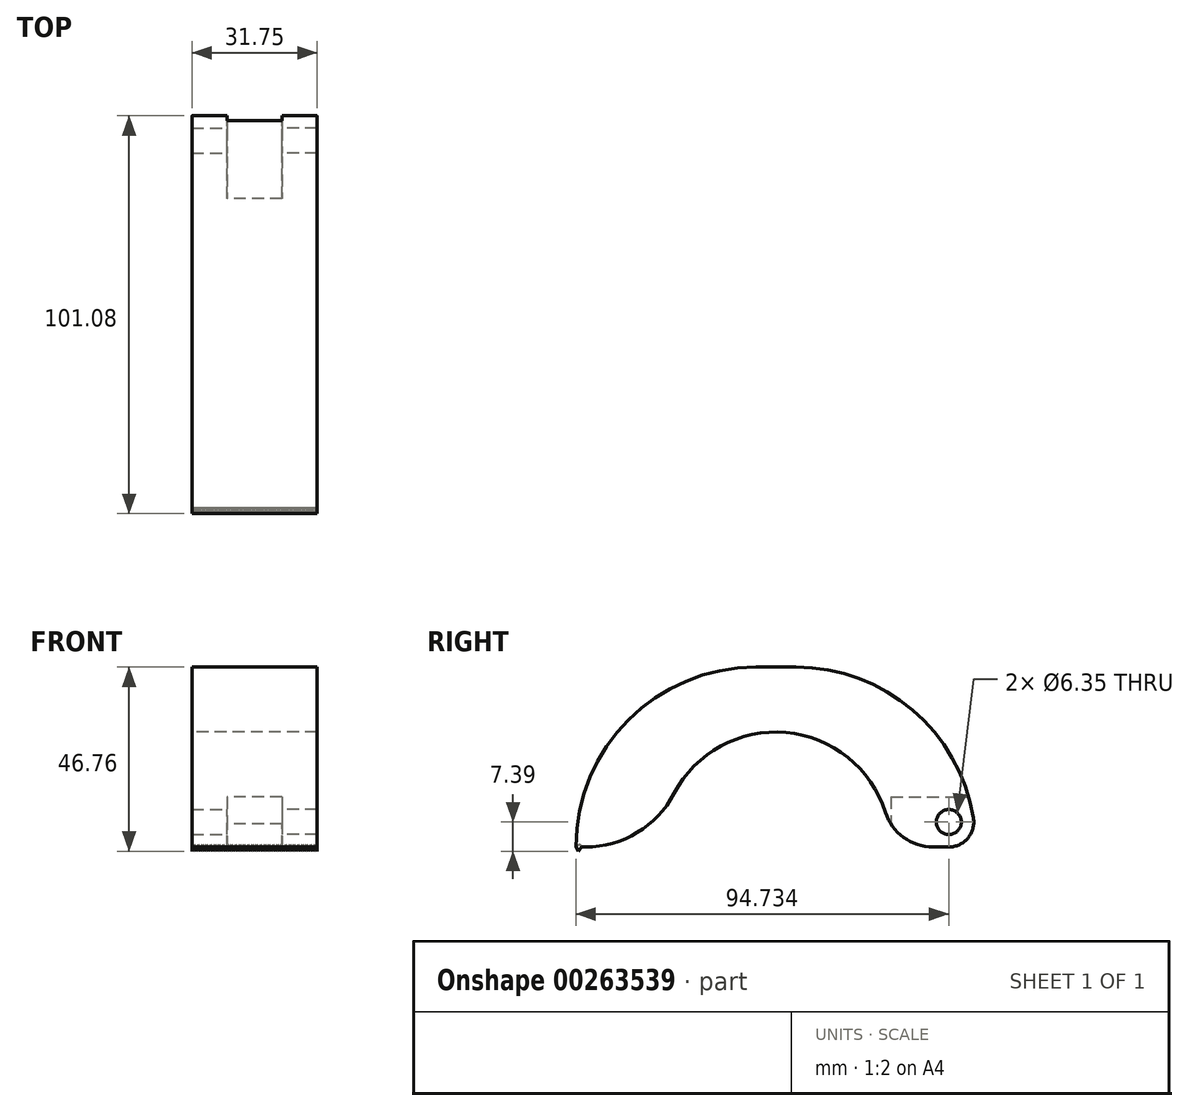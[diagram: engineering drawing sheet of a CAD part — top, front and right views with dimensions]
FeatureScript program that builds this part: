
annotation { "Feature Type Name" : "Feature", "Feature Type Description" : "" }
export const myFeature = defineFeature(function(context is Context, id is Id, definition is map)
    precondition{}
    {
        {
            var Q0;
            Q0=qCreatedBy(makeId("Right.planeOp"),FACE);
            var sketch = newSketch(context, id + "F0", { "sketchPlane" : qUnion([Q0])});
            skLineSegment(sketch, "E0.bottom", {"start": v(-5.08, 22.86) * mm, "end": v(5.08, 22.86) * mm});
            skLineSegment(sketch, "E0.top", {"start": v(-50.8, -22.86) * mm, "end": v(-48.34, -22.86) * mm});
            skLineSegment(sketch, "E0.left", {"start": v(-50.8, -22.86) * mm, "end": v(-50.8, -22.86) * mm});
            skLineSegment(sketch, "E0.right", {"start": v(50.8, -22.86) * mm, "end": v(50.8, -22.86) * mm});
            skPoint(sketch, "E0.middle", {"position": v(0, 0) * mm});
            skArc(sketch, "E1", {"start": v(27.84, -14) * mm, "mid": v(2.57, 6.24) * mm, "end": v(-25.86, -9.27) * mm});
            skLineSegment(sketch, "E2.trimOffspring", {"start": v(39.94, -22.86) * mm, "end": v(50.8, -22.86) * mm});
            skLineSegment(sketch, "E3", {"start": v(50.8, -22.86) * mm, "end": v(-50.8, -22.86) * mm, "construction": true});
            skPoint(sketch, "E4.visualSharp", {"position": v(50.8, 22.86) * mm});
            skArc(sketch, "E4.filletArc", {"start": v(50.8, -22.86) * mm, "mid": v(37.4, 9.47) * mm, "end": v(5.08, 22.86) * mm});
            skPoint(sketch, "E5.visualSharp", {"position": v(-50.8, 22.86) * mm});
            skArc(sketch, "E5.filletArc", {"start": v(-5.08, 22.86) * mm, "mid": v(-37.4, 9.47) * mm, "end": v(-50.8, -22.86) * mm});
            skPoint(sketch, "E6.visualSharp", {"position": v(29.21, -22.86) * mm});
            skArc(sketch, "E6.filletArc", {"start": v(27.84, -14) * mm, "mid": v(32.44, -20.41) * mm, "end": v(39.94, -22.86) * mm});
            skPoint(sketch, "E7.visualSharp", {"position": v(-29.2, -22.86) * mm});
            skArc(sketch, "E7.filletArc", {"start": v(-48.34, -22.86) * mm, "mid": v(-35.2, -19.2) * mm, "end": v(-25.86, -9.27) * mm});
            skLineSegment(sketch, "E8", {"start": v(-50.8, -22.86) * mm, "end": v(-50.07, -23.9) * mm});
            skLineSegment(sketch, "E9", {"start": v(-50.07, -23.9) * mm, "end": v(-49.34, -22.86) * mm});
            skSolve(sketch);
        }
        {
            var Q0;
            Q0 = qSketchRegion(id + "F0", true);
            extrude(context, id + "F1", {"entities" : qUnion([Q0]), "depth" : 31.75 * mm});
        }
        {
            var Q0;
            Q0=makeQuery(id+"F1.opExtrude","SWEPT_EDGE",EDGE,{"disambiguationData":[OSD([sQuery(id+"F0.wireOp",EDGE,"E2.trimOffspring"),sQuery(id+"F0.wireOp",EDGE,"E4.filletArc")])]});
            fillet(context, id + "F2", {"entities" : qUnion([Q0]), "radius" : 6.35 * mm, "tangentPropagation" : true, "allowEdgeOverflow" : false});
        }
        {
            var Q0;
            Q0=makeQuery(id+"F1.opExtrude","SWEPT_FACE",FACE,{"disambiguationData":[OSD([sQuery(id+"F0.wireOp",EDGE,"E2.trimOffspring")])]});
            var sketch = newSketch(context, id + "F3", { "sketchPlane" : qUnion([Q0])});
            skLineSegment(sketch, "E10", {"start": v(0, -41.94) * mm, "end": v(31.75, -41.94) * mm, "construction": true});
            skLineSegment(sketch, "E11", {"start": v(15.88, -43.93) * mm, "end": v(15.88, -39.94) * mm, "construction": true});
            skLineSegment(sketch, "E12.bottom", {"start": v(8.9, -29.24) * mm, "end": v(22.86, -29.24) * mm});
            skLineSegment(sketch, "E12.top", {"start": v(8.9, -54.64) * mm, "end": v(22.86, -54.64) * mm});
            skLineSegment(sketch, "E12.left", {"start": v(8.9, -29.24) * mm, "end": v(8.9, -54.64) * mm});
            skLineSegment(sketch, "E12.right", {"start": v(22.86, -29.24) * mm, "end": v(22.86, -54.64) * mm});
            skPoint(sketch, "E12.middle", {"position": v(15.88, -41.94) * mm});
            skSolve(sketch);
        }
        {
            var Q0;
            Q0 = qSketchRegion(id + "F3", true);
            extrude(context, id + "F4", {"entities" : qUnion([Q0]), "operationType" : NewBodyOperationType.REMOVE, "oppositeDirection" : true, "depth" : 12.7 * mm});
        }
        {
            var Q0;
            Q0=makeQuery(id+"F4.boolean.opBoolean","COPY",FACE,{"derivedFrom":makeQuery(id+"F4.opExtrude","SWEPT_FACE",FACE,{"disambiguationData":[OSD([sQuery(id+"F3.wireOp",EDGE,"E12.left")])]})});
            var sketch = newSketch(context, id + "F5", { "sketchPlane" : qUnion([Q0])});
            skCircle(sketch, "E13", {"center": v(43.93, -16.5) * mm, "radius": 3.18 * mm});
            skSolve(sketch);
        }
        {
            var Q0;
            Q0=makeQuery(id+"F5.imprint","IMPRINT",FACE,{"disambiguationData":[TD([[makeQuery(id+"F5.imprint","IMPRINT",EDGE,{"derivedFrom":sQuery(id+"F5.wireOp",EDGE,"E13")}),1.0]])]});
            extrude(context, id + "F6", {"entities" : qUnion([Q0]), "operationType" : NewBodyOperationType.REMOVE, "endBound" : BoundingType.THROUGH_ALL, "oppositeDirection" : true, "depth" : 25.4 * mm});
        }
        {
            var Q0;
            Q0=makeQuery(id+"F4.boolean.opBoolean","COPY",FACE,{"derivedFrom":makeQuery(id+"F4.opExtrude","SWEPT_FACE",FACE,{"disambiguationData":[OSD([sQuery(id+"F3.wireOp",EDGE,"E12.right")])]})});
            var sketch = newSketch(context, id + "F7", { "sketchPlane" : qUnion([Q0])});
            skCircle(sketch, "E14", {"center": v(-43.93, -16.51) * mm, "radius": 3.18 * mm});
            skSolve(sketch);
        }
        {
            var Q0;
            Q0=makeQuery(id+"F7.imprint","IMPRINT",FACE,{"disambiguationData":[TD([[makeQuery(id+"F7.imprint","IMPRINT",EDGE,{"derivedFrom":sQuery(id+"F7.wireOp",EDGE,"E14")}),1.0]])]});
            extrude(context, id + "F8", {"entities" : qUnion([Q0]), "operationType" : NewBodyOperationType.REMOVE, "endBound" : BoundingType.THROUGH_ALL, "oppositeDirection" : true, "depth" : 25.4 * mm});
        }
        {
            var Q0;
            Q0=makeQuery(id+"F1.opExtrude","SWEPT_FACE",FACE,{"disambiguationData":[OSD([sQuery(id+"F0.wireOp",EDGE,"E8")])]});
            var sketch = newSketch(context, id + "F9", { "sketchPlane" : qUnion([Q0])});
            skLineSegment(sketch, "E15", {"start": v(0, 9.14) * mm, "end": v(1.06, 9.14) * mm});
            skLineSegment(sketch, "E16", {"start": v(1.06, 9.14) * mm, "end": v(2.12, 9.14) * mm});
            skLineSegment(sketch, "E17", {"start": v(2.12, 9.14) * mm, "end": v(3.18, 9.14) * mm});
            skLineSegment(sketch, "E18", {"start": v(3.18, 9.14) * mm, "end": v(4.23, 9.14) * mm});
            skLineSegment(sketch, "E19", {"start": v(4.23, 9.14) * mm, "end": v(5.3, 9.14) * mm});
            skLineSegment(sketch, "E20", {"start": v(5.3, 9.14) * mm, "end": v(6.35, 9.14) * mm});
            skLineSegment(sketch, "E21", {"start": v(6.35, 9.14) * mm, "end": v(7.4, 9.14) * mm});
            skLineSegment(sketch, "E22", {"start": v(7.4, 9.14) * mm, "end": v(8.47, 9.14) * mm});
            skLineSegment(sketch, "E23", {"start": v(8.47, 9.14) * mm, "end": v(9.52, 9.14) * mm});
            skLineSegment(sketch, "E24", {"start": v(10.58, 9.14) * mm, "end": v(11.64, 9.14) * mm});
            skLineSegment(sketch, "E25", {"start": v(25.4, 9.14) * mm, "end": v(26.46, 9.14) * mm});
            skLineSegment(sketch, "E26", {"start": v(26.46, 9.14) * mm, "end": v(27.52, 9.14) * mm});
            skLineSegment(sketch, "E27", {"start": v(27.52, 9.14) * mm, "end": v(28.58, 9.14) * mm});
            skLineSegment(sketch, "E28", {"start": v(28.58, 9.14) * mm, "end": v(29.63, 9.14) * mm});
            skLineSegment(sketch, "E29", {"start": v(29.63, 9.14) * mm, "end": v(30.7, 9.14) * mm});
            skLineSegment(sketch, "E30", {"start": v(30.7, 9.14) * mm, "end": v(31.75, 9.14) * mm});
            skLineSegment(sketch, "E31", {"start": v(9.52, 9.14) * mm, "end": v(10.58, 9.14) * mm});
            skLineSegment(sketch, "E32", {"start": v(24.34, 9.14) * mm, "end": v(25.4, 9.14) * mm});
            skLineSegment(sketch, "E33", {"start": v(0, 9.14) * mm, "end": v(0.53, 10.41) * mm});
            skLineSegment(sketch, "E34", {"start": v(0.53, 10.41) * mm, "end": v(1.06, 9.14) * mm});
            skLineSegment(sketch, "E35", {"start": v(1.06, 9.14) * mm, "end": v(1.59, 10.41) * mm});
            skLineSegment(sketch, "E36", {"start": v(1.59, 10.41) * mm, "end": v(2.12, 9.14) * mm});
            skLineSegment(sketch, "E37", {"start": v(2.12, 9.14) * mm, "end": v(2.65, 10.41) * mm});
            skLineSegment(sketch, "E38", {"start": v(2.65, 10.41) * mm, "end": v(3.18, 9.14) * mm});
            skLineSegment(sketch, "E39", {"start": v(3.18, 9.14) * mm, "end": v(3.7, 10.41) * mm});
            skLineSegment(sketch, "E40", {"start": v(3.7, 10.41) * mm, "end": v(4.23, 9.14) * mm});
            skLineSegment(sketch, "E41", {"start": v(4.23, 9.14) * mm, "end": v(4.76, 10.41) * mm});
            skLineSegment(sketch, "E42", {"start": v(4.76, 10.41) * mm, "end": v(5.3, 9.14) * mm});
            skLineSegment(sketch, "E43", {"start": v(5.3, 9.14) * mm, "end": v(5.82, 10.41) * mm});
            skLineSegment(sketch, "E44", {"start": v(5.82, 10.41) * mm, "end": v(6.35, 9.14) * mm});
            skLineSegment(sketch, "E45", {"start": v(6.35, 9.14) * mm, "end": v(6.88, 10.41) * mm});
            skLineSegment(sketch, "E46", {"start": v(6.88, 10.41) * mm, "end": v(7.4, 9.14) * mm});
            skLineSegment(sketch, "E47", {"start": v(7.4, 9.14) * mm, "end": v(7.94, 10.41) * mm});
            skLineSegment(sketch, "E48", {"start": v(7.94, 10.41) * mm, "end": v(8.47, 9.14) * mm});
            skLineSegment(sketch, "E49", {"start": v(8.47, 9.14) * mm, "end": v(9, 10.41) * mm});
            skLineSegment(sketch, "E50", {"start": v(9, 10.41) * mm, "end": v(9.53, 9.14) * mm});
            skLineSegment(sketch, "E51", {"start": v(9.53, 9.14) * mm, "end": v(10.05, 10.41) * mm});
            skLineSegment(sketch, "E52", {"start": v(10.05, 10.41) * mm, "end": v(10.58, 9.14) * mm});
            skLineSegment(sketch, "E53", {"start": v(25.4, 9.14) * mm, "end": v(25.93, 10.41) * mm});
            skLineSegment(sketch, "E54", {"start": v(25.93, 10.41) * mm, "end": v(26.46, 9.14) * mm});
            skLineSegment(sketch, "E55", {"start": v(26.46, 9.14) * mm, "end": v(26.99, 10.41) * mm});
            skLineSegment(sketch, "E56", {"start": v(26.99, 10.41) * mm, "end": v(27.52, 9.14) * mm});
            skLineSegment(sketch, "E57", {"start": v(27.52, 9.14) * mm, "end": v(28.05, 10.41) * mm});
            skLineSegment(sketch, "E58", {"start": v(28.05, 10.41) * mm, "end": v(28.58, 9.14) * mm});
            skLineSegment(sketch, "E59", {"start": v(28.58, 9.14) * mm, "end": v(29.1, 10.41) * mm});
            skPoint(sketch, "E59.endSnap0", {"position": v(29.1, 9.14) * mm});
            skLineSegment(sketch, "E60", {"start": v(29.1, 10.41) * mm, "end": v(29.63, 9.14) * mm});
            skLineSegment(sketch, "E61", {"start": v(29.63, 9.14) * mm, "end": v(30.16, 10.41) * mm});
            skLineSegment(sketch, "E62", {"start": v(30.16, 10.41) * mm, "end": v(30.7, 9.14) * mm});
            skLineSegment(sketch, "E63", {"start": v(30.7, 9.14) * mm, "end": v(31.22, 10.41) * mm});
            skLineSegment(sketch, "E64", {"start": v(31.22, 10.41) * mm, "end": v(31.75, 9.14) * mm});
            skLineSegment(sketch, "E65", {"start": v(10.58, 9.14) * mm, "end": v(11.11, 10.41) * mm});
            skLineSegment(sketch, "E66", {"start": v(11.11, 10.41) * mm, "end": v(11.64, 9.14) * mm});
            skLineSegment(sketch, "E67", {"start": v(24.34, 9.14) * mm, "end": v(24.87, 10.41) * mm});
            skLineSegment(sketch, "E68", {"start": v(24.87, 10.41) * mm, "end": v(25.4, 9.14) * mm});
            skLineSegment(sketch, "E69", {"start": v(11.64, 9.14) * mm, "end": v(12.17, 10.41) * mm});
            skLineSegment(sketch, "E70", {"start": v(12.17, 10.41) * mm, "end": v(12.7, 9.14) * mm});
            skLineSegment(sketch, "E71", {"start": v(12.7, 9.14) * mm, "end": v(13.23, 10.41) * mm});
            skLineSegment(sketch, "E72", {"start": v(13.23, 10.41) * mm, "end": v(13.76, 9.14) * mm});
            skLineSegment(sketch, "E73", {"start": v(13.76, 9.14) * mm, "end": v(14.29, 10.41) * mm});
            skLineSegment(sketch, "E74", {"start": v(14.29, 10.41) * mm, "end": v(14.82, 9.14) * mm});
            skLineSegment(sketch, "E75", {"start": v(14.82, 9.14) * mm, "end": v(15.35, 10.41) * mm});
            skLineSegment(sketch, "E76", {"start": v(15.35, 10.41) * mm, "end": v(15.88, 9.14) * mm});
            skLineSegment(sketch, "E77", {"start": v(15.88, 9.14) * mm, "end": v(16.4, 10.41) * mm});
            skLineSegment(sketch, "E78", {"start": v(16.4, 10.41) * mm, "end": v(16.93, 9.14) * mm});
            skLineSegment(sketch, "E79", {"start": v(16.93, 9.14) * mm, "end": v(17.46, 10.41) * mm});
            skLineSegment(sketch, "E80", {"start": v(17.46, 10.41) * mm, "end": v(18, 9.14) * mm});
            skLineSegment(sketch, "E81", {"start": v(18, 9.14) * mm, "end": v(18.52, 10.41) * mm});
            skLineSegment(sketch, "E82", {"start": v(18.52, 10.41) * mm, "end": v(19.05, 9.14) * mm});
            skLineSegment(sketch, "E83", {"start": v(19.05, 9.14) * mm, "end": v(19.58, 10.41) * mm});
            skLineSegment(sketch, "E84", {"start": v(19.58, 10.41) * mm, "end": v(20.1, 9.14) * mm});
            skLineSegment(sketch, "E85", {"start": v(20.1, 9.14) * mm, "end": v(20.64, 10.41) * mm});
            skLineSegment(sketch, "E86", {"start": v(20.64, 10.41) * mm, "end": v(21.17, 9.14) * mm});
            skLineSegment(sketch, "E87", {"start": v(21.17, 9.14) * mm, "end": v(21.7, 10.41) * mm});
            skLineSegment(sketch, "E88", {"start": v(21.7, 10.41) * mm, "end": v(22.23, 9.14) * mm});
            skLineSegment(sketch, "E89", {"start": v(22.22, 9.14) * mm, "end": v(22.75, 10.41) * mm});
            skLineSegment(sketch, "E90", {"start": v(22.75, 10.41) * mm, "end": v(23.28, 9.14) * mm});
            skLineSegment(sketch, "E91", {"start": v(23.28, 9.14) * mm, "end": v(23.81, 10.41) * mm});
            skLineSegment(sketch, "E92", {"start": v(23.81, 10.41) * mm, "end": v(24.34, 9.14) * mm});
            skLineSegment(sketch, "E93", {"start": v(11.64, 9.14) * mm, "end": v(12.7, 9.14) * mm});
            skLineSegment(sketch, "E94", {"start": v(12.7, 9.14) * mm, "end": v(13.76, 9.14) * mm});
            skLineSegment(sketch, "E95", {"start": v(14.82, 9.14) * mm, "end": v(13.76, 9.14) * mm});
            skLineSegment(sketch, "E96", {"start": v(14.82, 9.14) * mm, "end": v(15.88, 9.14) * mm});
            skLineSegment(sketch, "E97", {"start": v(15.88, 9.14) * mm, "end": v(16.93, 9.14) * mm});
            skLineSegment(sketch, "E98", {"start": v(24.34, 9.14) * mm, "end": v(23.28, 9.14) * mm});
            skLineSegment(sketch, "E99", {"start": v(23.28, 9.14) * mm, "end": v(22.22, 9.14) * mm});
            skLineSegment(sketch, "E100", {"start": v(22.22, 9.14) * mm, "end": v(21.17, 9.14) * mm});
            skLineSegment(sketch, "E101", {"start": v(21.17, 9.14) * mm, "end": v(20.1, 9.14) * mm});
            skLineSegment(sketch, "E102", {"start": v(18, 9.14) * mm, "end": v(16.93, 9.14) * mm});
            skLineSegment(sketch, "E103", {"start": v(19.05, 9.14) * mm, "end": v(18, 9.14) * mm});
            skLineSegment(sketch, "E104", {"start": v(20.1, 9.14) * mm, "end": v(19.05, 9.14) * mm});
            skSolve(sketch);
        }
        {
            var Q0;
            Q0 = qSketchRegion(id + "F9", true);
            extrude(context, id + "F10", {"entities" : qUnion([Q0]), "operationType" : NewBodyOperationType.REMOVE, "oppositeDirection" : true, "depth" : 1.27 * mm});
        }
    });
